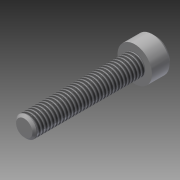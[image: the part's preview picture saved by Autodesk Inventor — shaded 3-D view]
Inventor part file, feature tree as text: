
AUTODESK INVENTOR PART (.ipt)
format: ipt  version: 2014 SP1 (Build 180222100, 222)  size: 92,672 bytes
history: native  units: in
note: dims shown in document units (in); Inventor stores cm internally (conversion verified against a paired STEP export)
features: other x2, thread x1, imported_body x1
ambient origin geometry x8: Origin, YZ Plane, XZ Plane, XY Plane, X Axis, Y Axis, Z Axis, Center Point
bodies: Body1 (feature_tree)
feature tree (4):
  other  "10-32x1000shcs"
  other  "10-32x1000shcs1"
  thread  "Thread1"  [1 undecoded]
  imported_body  "Base1"
note: 1 required parameter value undecoded (feature->parameter linkage not recoverable at this tier; creation-order binding heuristic only, values carry confidence <= 0.55)
